AUTODESK INVENTOR PART (.ipt)
format: ipt  version: 2022 (Build 260153000, 153)  size: 145,408 bytes
history: native  units: mm (DEFAULTED — no unit token found)
features: other x4, sketch x3, plane x2, extrude x1, split x1
ambient origin geometry x8: Origin, YZ Plane, XZ Plane, XY Plane, X Axis, Y Axis, Z Axis, Center Point
bodies: Solid1 (feature_tree)
feature tree (11):
  parser-record x1  (decoder bookkeeping rows leaked as tree rows — omitted from the tree; the rows remain in map.json)
  other  "Driven Length"
  other  "Plano inicial"
  other  "Plano final"
  extrude  "Cuerpo"  TaperAngle=0.0deg  [1 undecoded]
  plane  "Plano de trabajo4"
  split  "Dividir1"
  sketch  "Boceto"  dims[d10=40.0mm d11=40.0mm d12=5.0mm d13=-0.0mm d14=311.768067mm d15=20.0mm d16=20.0mm d17=90.0deg d18=311.768067mm]
  sketch  "Sketch3"  dims[d3=311.768067mm d4=0.0mm]
  plane  "Work Plane3"
  sketch  "Sketch4"  dims[d7=7.5mm]
note: 1 required parameter value undecoded (feature->parameter linkage not recoverable at this tier; creation-order binding heuristic only, values carry confidence <= 0.55)
